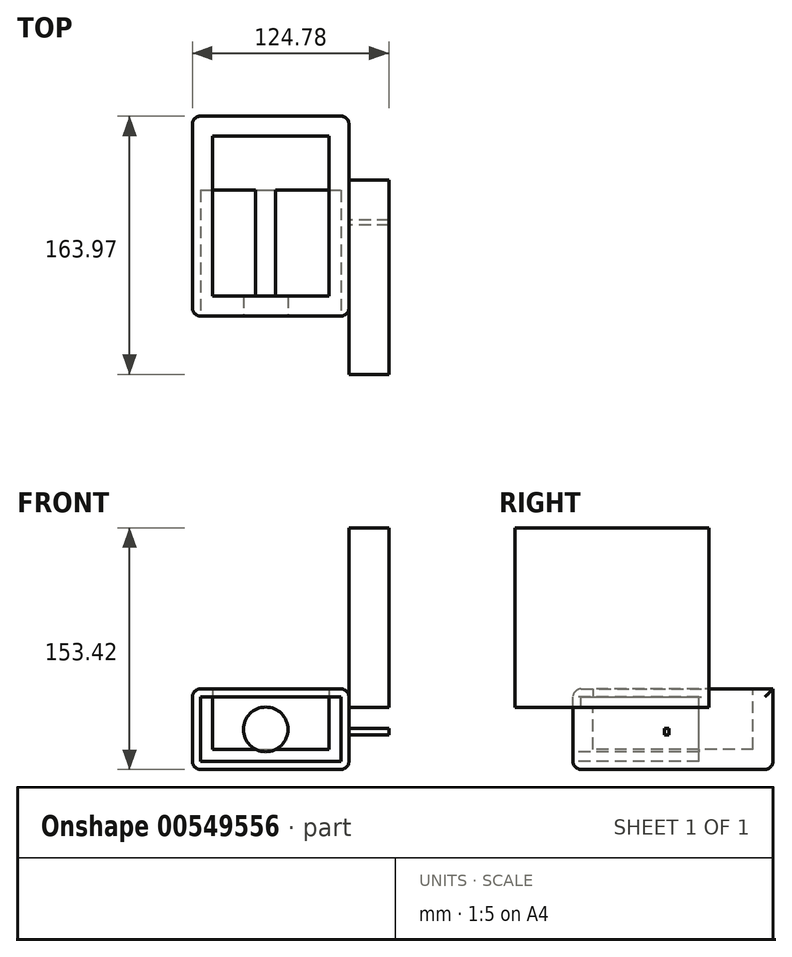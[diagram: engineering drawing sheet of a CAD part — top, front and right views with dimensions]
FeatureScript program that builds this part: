
annotation { "Feature Type Name" : "Feature", "Feature Type Description" : "" }
export const myFeature = defineFeature(function(context is Context, id is Id, definition is map)
    precondition{}
    {
        {
            var Q0;
            Q0=qCreatedBy(makeId("Front.planeOp"),FACE);
            var sketch = newSketch(context, id + "F0", { "sketchPlane" : qUnion([Q0])});
            skLineSegment(sketch, "E0.bottom", {"start": v(0, 0) * mm, "end": v(54.22, 0) * mm});
            skLineSegment(sketch, "E0.top", {"start": v(0, 51.1) * mm, "end": v(54.22, 51.1) * mm});
            skLineSegment(sketch, "E0.left", {"start": v(0, 0) * mm, "end": v(0, 51.1) * mm});
            skLineSegment(sketch, "E0.right", {"start": v(54.22, 0) * mm, "end": v(54.22, 51.1) * mm});
            skSolve(sketch);
        }
        {
            var Q0;
            Q0=makeQuery(id+"F0.imprint","IMPRINT",FACE,{"disambiguationData":[TD([[makeQuery(id+"F0.imprint","IMPRINT",EDGE,{"derivedFrom":sQuery(id+"F0.wireOp",EDGE,"E0.bottom")}),1.0]])]});
            extrude(context, id + "F1", {"entities" : qUnion([Q0]), "depth" : 127 * mm, "offsetDistance" : 25.4 * mm});
        }
        {
            var Q0;
            Q0=makeQuery(id+"F1.opExtrude","SWEPT_FACE",FACE,{"disambiguationData":[OSD([sQuery(id+"F0.wireOp",EDGE,"E0.left")])]});
            extrude(context, id + "F2", {"entities" : qUnion([Q0]), "operationType" : NewBodyOperationType.ADD, "depth" : 45.16 * mm, "offsetDistance" : 25.4 * mm});
        }
        {
            var Q0;
            Q0=makeQuery(id+"F1.opExtrude","SWEPT_FACE",FACE,{"disambiguationData":[OSD([sQuery(id+"F0.wireOp",EDGE,"E0.right")])]});
            var Q1;
            {var subQ0=sQuery(id+"F0.wireOp",EDGE,"E0.bottom");Q1=makeQuery(id+"F2.boolean.opBoolean","MERGE",FACE,{"derivedFrom":[makeQuery(id+"F1.opExtrude","SWEPT_FACE",FACE,{"disambiguationData":[OSD([subQ0])]}),makeQuery(id+"F2.opExtrude","SWEPT_FACE",FACE,{"disambiguationData":[OSD([subQ0,sQuery(id+"F0.wireOp",EDGE,"E0.left")])]})]});}
            var Q2;
            {var subQ0=sQuery(id+"F0.wireOp",EDGE,"E0.left");Q2=makeQuery(id+"F2.boolean.opBoolean","MERGE",FACE,{"derivedFrom":[makeQuery(id+"F1.opExtrude","CAP_FACE",FACE,{"disambiguationData":[OSD([sQuery(id+"F0.wireOp",EDGE,"E0.bottom"),sQuery(id+"F0.wireOp",EDGE,"E0.top"),subQ0,sQuery(id+"F0.wireOp",EDGE,"E0.right")])],"isStart":false}),makeQuery(id+"F2.opExtrude","SWEPT_FACE",FACE,{"disambiguationData":[OSD([subQ0]),TDD([makeQuery(id+"F1.opExtrude","CAP_EDGE",EDGE,{"disambiguationData":[OSD([subQ0])],"isStart":false})])]})]});}
            var Q3;
            Q3=makeQuery(id+"F2.opExtrude","CAP_FACE",FACE,{"disambiguationData":[OSD([sQuery(id+"F0.wireOp",EDGE,"E0.left")])],"isStart":false});
            fillet(context, id + "F3", {"entities" : qUnion([Q0, Q1, Q2, Q3]), "radius" : 5.08 * mm, "tangentPropagation" : true, "allowEdgeOverflow" : false});
        }
        {
            var Q0;
            {var subQ0=sQuery(id+"F0.wireOp",EDGE,"E0.top");Q0=makeQuery(id+"F2.boolean.opBoolean","MERGE",FACE,{"derivedFrom":[makeQuery(id+"F1.opExtrude","SWEPT_FACE",FACE,{"disambiguationData":[OSD([subQ0])]}),makeQuery(id+"F2.opExtrude","SWEPT_FACE",FACE,{"disambiguationData":[OSD([subQ0,sQuery(id+"F0.wireOp",EDGE,"E0.left")])]})]});}
            shell(context, id + "F4", {"entities" : qUnion([Q0]), "thickness" : 12.7 * mm});
        }
        {
            var Q0;
            {var subQ0=sQuery(id+"F0.wireOp",EDGE,"E0.left");Q0=makeQuery(id+"F2.boolean.opBoolean","MERGE",FACE,{"derivedFrom":[makeQuery(id+"F1.opExtrude","CAP_FACE",FACE,{"disambiguationData":[OSD([sQuery(id+"F0.wireOp",EDGE,"E0.bottom"),sQuery(id+"F0.wireOp",EDGE,"E0.top"),subQ0,sQuery(id+"F0.wireOp",EDGE,"E0.right")])],"isStart":false}),makeQuery(id+"F2.opExtrude","SWEPT_FACE",FACE,{"disambiguationData":[OSD([subQ0]),TDD([makeQuery(id+"F1.opExtrude","CAP_EDGE",EDGE,{"disambiguationData":[OSD([subQ0])],"isStart":false})])]})]});}
            var sketch = newSketch(context, id + "F5", { "sketchPlane" : qUnion([Q0])});
            skCircle(sketch, "E1", {"center": v(1.36, 25.38) * mm, "radius": 14.18 * mm});
            skSolve(sketch);
        }
        {
            var Q0;
            Q0=makeQuery(id+"F5.imprint","IMPRINT",FACE,{"disambiguationData":[TD([[makeQuery(id+"F5.imprint","IMPRINT",EDGE,{"derivedFrom":sQuery(id+"F5.wireOp",EDGE,"E1")}),-1.0]])]});
            extrude(context, id + "F6", {"entities" : qUnion([Q0]), "operationType" : NewBodyOperationType.REMOVE, "oppositeDirection" : true, "depth" : 79.96 * mm, "offsetDistance" : 25.4 * mm});
        }
        {
            var Q0;
            Q0=makeQuery(id+"F1.opExtrude","SWEPT_FACE",FACE,{"disambiguationData":[OSD([sQuery(id+"F0.wireOp",EDGE,"E0.right")])]});
            var sketch = newSketch(context, id + "F7", { "sketchPlane" : qUnion([Q0])});
            skLineSegment(sketch, "E2.bottom", {"start": v(-69.1, 25.98) * mm, "end": v(-65.95, 25.98) * mm});
            skLineSegment(sketch, "E2.top", {"start": v(-69.1, 21.94) * mm, "end": v(-65.95, 21.94) * mm});
            skLineSegment(sketch, "E2.left", {"start": v(-69.1, 25.98) * mm, "end": v(-69.1, 21.94) * mm});
            skLineSegment(sketch, "E2.right", {"start": v(-65.95, 25.98) * mm, "end": v(-65.95, 21.94) * mm});
            skLineSegment(sketch, "E3.bottom", {"start": v(-40.64, 39.3) * mm, "end": v(-163.97, 39.3) * mm});
            skLineSegment(sketch, "E3.top", {"start": v(-40.64, 153.42) * mm, "end": v(-163.97, 153.42) * mm});
            skLineSegment(sketch, "E3.left", {"start": v(-40.64, 39.3) * mm, "end": v(-40.64, 153.42) * mm});
            skLineSegment(sketch, "E3.right", {"start": v(-163.97, 39.3) * mm, "end": v(-163.97, 153.42) * mm});
            skSolve(sketch);
        }
        {
            var Q0;
            Q0 = qSketchRegion(id + "F7", true);
            extrude(context, id + "F8", {"entities" : qUnion([Q0]), "operationType" : NewBodyOperationType.ADD, "depth" : 25.4 * mm, "offsetDistance" : 25.4 * mm});
        }
    });
